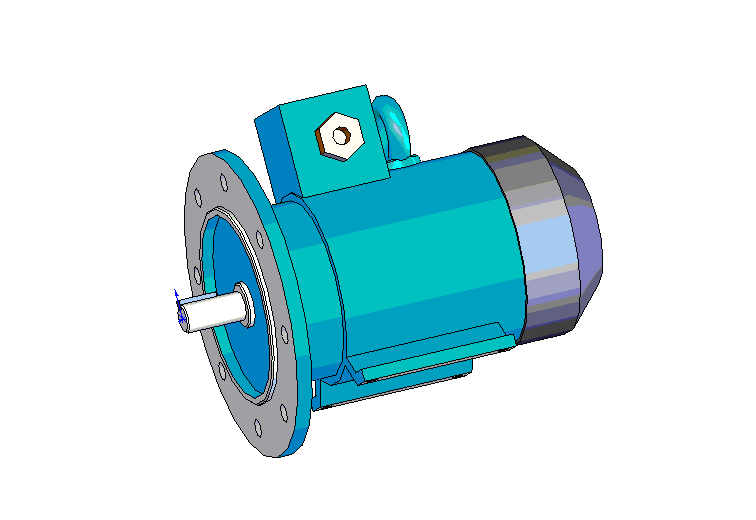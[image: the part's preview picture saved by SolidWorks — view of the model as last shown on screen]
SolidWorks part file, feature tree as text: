
SOLIDWORKS PART (.sldprt)
format: sldprt  version: not decoded by parser v0  size: 563,200 bytes
history: native  units: mm
features: sketch x18, extrude x12, chamfer x5, plane x4, cut_extrude x4, material x1, sweep x1 (+10 scaffold rows collapsed)
feature tree (55):
  scaffold x10  (default folders/planes/origin — collapsed)
  material  "Ст.3 ГОСТ 380-88"
  plane  "Спереди"
  plane  "Сверху"
  plane  "Справа"
  sketch  "Эскиз2"  dims[D1=19.0mm]
  extrude  "Вытянуть1"  Depth=40mm
  sketch  "Эскиз3"  dims[D1=6.0mm D2=6.0mm D3=21.5mm]
  extrude  "Вытянуть2"  Depth=25mm
  chamfer  "Фаска1"  Distance=1mm Angle=45deg
  sketch  "Эскиз4"  dims[D1=200.0mm]
  extrude  "Вытянуть3"  Depth=10mm
  sketch  "Эскиз5"  dims[D1=120.0mm D2=30.0mm]
  cut_extrude  "Вырез-Вытянуть1"  Depth=4mm
  sketch  "Эскиз7"  dims[D1=130.0mm D2=120.0mm]
  extrude  "Вытянуть4"  Depth=3.5mm
  chamfer  "Фаска2"  Distance=1mm Angle=45deg
  sketch  "Эскиз8"  dims[c1.D2=12.0mm c1.D1=~121.18096mm c2.D1=22.5deg c2.D3=82.5mm c2.D4=82.5mm c2.D5=82.5mm]
  cut_extrude  "Вырез-Вытянуть2"  [1 undecoded]
  chamfer  "Фаска3"  Distance=1mm Angle=45deg
  sketch  "Эскиз9"  dims[D1=116.0mm]
  extrude  "Вытянуть5"  Depth=38mm
  sketch  "Эскиз10"  dims[D1=126.0mm]
  extrude  "Вытянуть6"  Depth=123mm
  sketch  "Эскиз11"  dims[D1=130.0mm]
  extrude  "Вытянуть7"  Depth=61.5mm
  chamfer  "Фаска4"  Distance=25mm Angle=45deg
  sketch  "Эскиз12"  dims[c1.D1=8.0mm c1.D2=8.0mm c1.D3=71.0mm c1.D4=8.0mm c1.D5=8.0mm c1.D6=~27.660663mm c2.D6=45.0deg c2.D7=~118.313813mm c3.D7=45.0deg c3.D8=126.0mm c3.D9=98.0mm c3.D10=49.0mm]
  extrude  "Вытянуть8"  Depth=104mm
  sketch  "Эскиз13"  dims[c1.D2=7.0mm c1.D6=7.0mm c1.D1=95.0mm c1.D3=56.0mm c1.D4=90.0deg c1.D5=185.0mm c2.D6=112.0mm c2.D7=90.0mm]
  cut_extrude  "Вырез-Вытянуть3"  [1 undecoded]
  sketch  "Эскиз14"  dims[D1=60.0mm D2=60.0mm D3=1.0mm]
  extrude  "Вытянуть9"  Depth=117mm
  sketch  "Эскиз15"  dims[D1=30.0mm D2=165.0mm]
  extrude  "Вытянуть10"  Depth=68mm
  chamfer  "Фаска5"  Distance=1mm Angle=45deg
  plane  "Плоскость1"  Offset=165mm
  sketch  "Эскиз16"  dims[D1=36.0mm]
  sketch  "Эскиз17"  dims[D1=14.0mm D2=165.0mm D3=36.0mm]
  sweep  "По траектории1"
  sketch  "Эскиз18"  dims[D1=18.0mm D2=30.0mm D3=30.0mm]
  extrude  "Вытянуть11"  Depth=8mm
  sketch  "Эскиз19"  dims[D1=~14.21506mm]
  extrude  "Вытянуть12"  Depth=10mm
  sketch  "Эскиз20"  dims[D1=12.0mm]
  cut_extrude  "Вырез-Вытянуть4"  Depth=10mm
decode coverage: 37 of 40 modeling features carry decoded parameters
note: ~ marks probable driven/reference dimensions
note: 2 parameter values undecoded
note: suppression state not decoded; provenance and decode notes live in map.json
